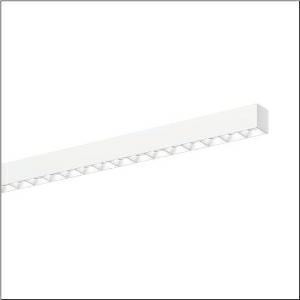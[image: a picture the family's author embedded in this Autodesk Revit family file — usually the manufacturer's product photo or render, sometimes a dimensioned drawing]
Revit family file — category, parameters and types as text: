
# Revit family: silica_r__21_51mx26db45wb_cce2
name_source: partatom
category: Lighting Fixtures
units: mm (PartAtom-declared; Revit-internal decimal feet)

## family parameters
Cut with Voids When Loaded = No
Host = Face
Light Source = No
Part Type = Normal
Room Calculation Point = No
Round Connector Dimension = Use Diameter
Shared = No

## types (1)
- --- (1 x LED, 5400 lm, 29.3 W, 4000K)
    Apparent Load = 29 VA
    CIE Flux Codes = 83 98 100 100 100
    Color Rendering = 80
    Color Temperature = 4000K
    Default Elevation = 1800 mm
    Description = Silica® 21, office luminaire, primary light control with darklight reflector, of PMMA, white, CAT 2 (L<= 3000cd/m²), light emission: direct distribution, primary light characteristic: symmetric, installation type: surface-mounted, LED, rated luminous flux: 5.400lm, luminous efficacy: 184lm/W, light colour: 840, colour temperature: 4000K, control gear: DALI 2, with terminal, 3+2-pole, max. 2.5mm², mains connection: 220..240V, AC, 50/60Hz, rated input power: 29.3W, luminaire housing, of aluminium, traffic white (RAL 9016), length: 1.504mm, width: 53mm, height: 53mm, protection rating (complete): IP20, insulation class (complete): insulation class I (protective earthing), certification: CE, permissible operating ambient temperature: 0..+35°C, standard: EN 50419, packaging unit: 1 piece
    Height = 53 mm
    Lamp = 1 x LED
    Lamp Light Flux = 5400 lm
    Lamp Power = 29.3 W
    Lamp count = 1
    Length = 1504 mm
    Luminous efficacy = 184 lm/W
    Manufacturer = Siteco
    ModVariant = No
    Model = 51MX26DB45WB
    Mounting Place = Ceiling
    Mounting Type = Surface mounted
    Number of Poles = 1
    OnlyDefault = Yes
    Power Factor = 1
    Product Name = Silica® 21
    Product group = office luminaire | ceiling mounted
    ProductGroupID = 302
    Protection Class = Protection class I
    Protection Degree = IP 20
    RLX_Detail_Level = 1
    RLX_Emergency_Light_Flux = 0 lm
    RLX_Emergency_Type = 0
    RLX_Emergency_Type_DB = No
    RlxData = <blob elided: 41869 chars, md5=a7bc8370>
    Socket = socket
    Standby Power = 0 W
    System Light Flux = 5400 lm
    System Power = 29 W
    Type Comments = factory setting: luminous flux: 100 % | dim-lin: 254 | 336 mA
    Type Image = l_1335934.jpg
    URL = http://relux.com
    VarID = @adj_124294
    Voltage = 0 V
    Weight = 0.00 kg
    Width = 53 mm

## geometry (parser evidence)
native form markers: Blend x4, Sweep x12
no freeform markers — native parametric forms only
